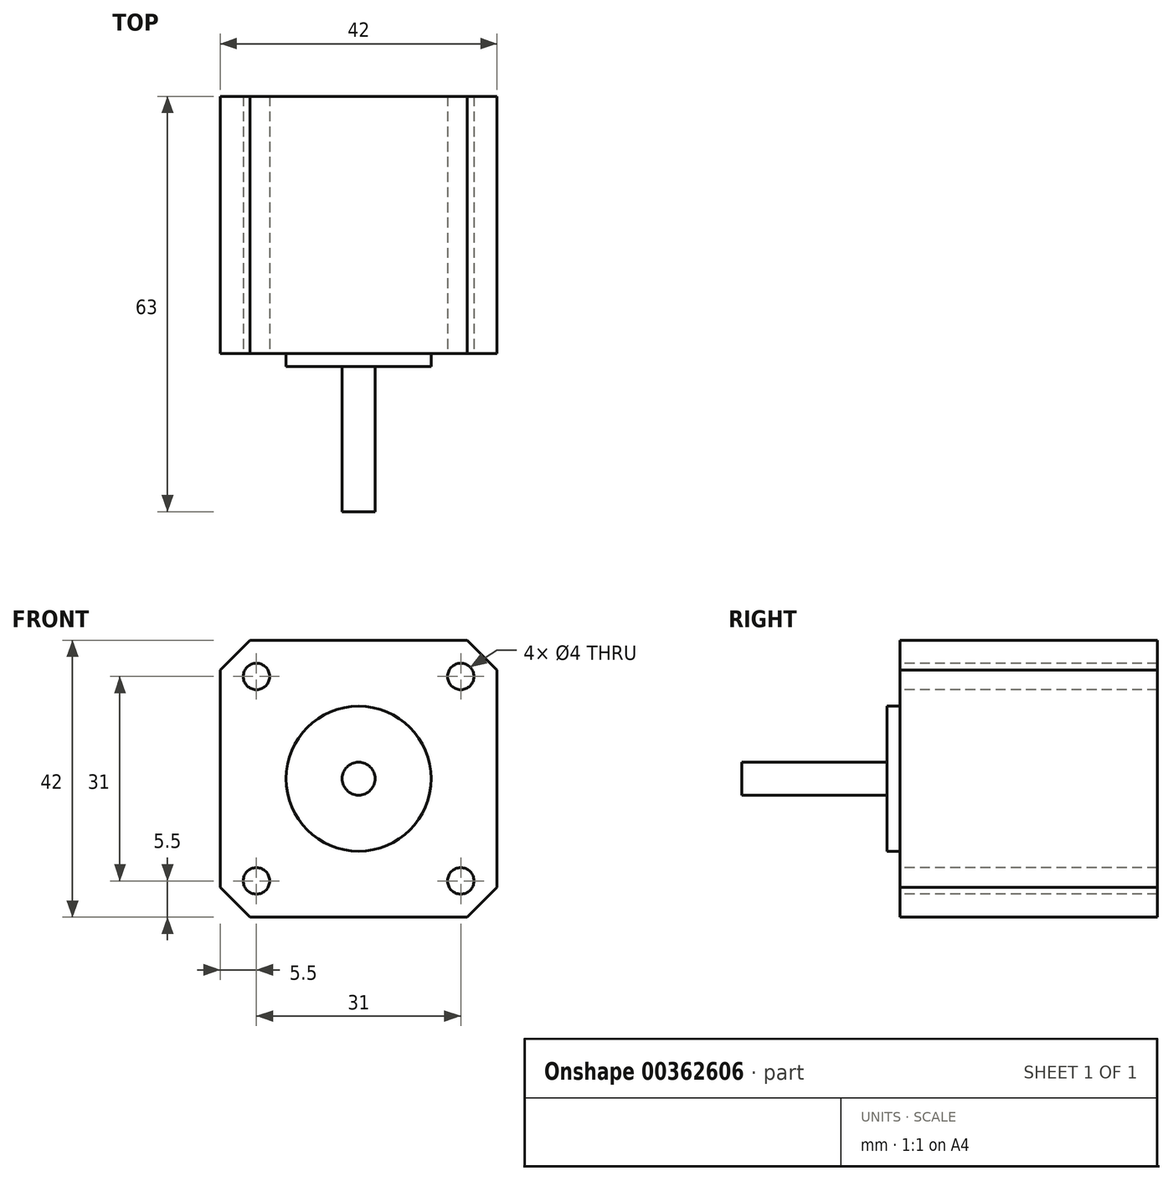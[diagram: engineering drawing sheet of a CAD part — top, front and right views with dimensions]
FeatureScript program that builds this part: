
annotation { "Feature Type Name" : "Feature", "Feature Type Description" : "" }
export const myFeature = defineFeature(function(context is Context, id is Id, definition is map)
    precondition{}
    {
        {
            var Q0;
            Q0=qCreatedBy(makeId("Front.planeOp"),FACE);
            var sketch = newSketch(context, id + "F0", { "sketchPlane" : qUnion([Q0])});
            skCircle(sketch, "E0", {"center": v(0, 0) * mm, "radius": 2.5 * mm});
            skSolve(sketch);
        }
        {
            var Q0;
            Q0=qCreatedBy(makeId("Front.planeOp"),FACE);
            var sketch = newSketch(context, id + "F1", { "sketchPlane" : qUnion([Q0])});
            skCircle(sketch, "E1", {"center": v(0, 0) * mm, "radius": 11 * mm});
            skSolve(sketch);
        }
        {
            var Q0;
            Q0=qCreatedBy(makeId("Front.planeOp"),FACE);
            var sketch = newSketch(context, id + "F2", { "sketchPlane" : qUnion([Q0])});
            skLineSegment(sketch, "E2.bottom", {"start": v(16.5, 21) * mm, "end": v(-16.5, 21) * mm});
            skLineSegment(sketch, "E2.top", {"start": v(16.5, -21) * mm, "end": v(-16.5, -21) * mm});
            skLineSegment(sketch, "E2.left", {"start": v(21, 16.5) * mm, "end": v(21, -16.5) * mm});
            skLineSegment(sketch, "E2.right", {"start": v(-21, 16.5) * mm, "end": v(-21, -16.5) * mm});
            skPoint(sketch, "E2.middle", {"position": v(0, 0) * mm});
            skPoint(sketch, "E3", {"position": v(-15.5, 15.5) * mm});
            skPoint(sketch, "E4", {"position": v(-15.5, -15.5) * mm});
            skPoint(sketch, "E5", {"position": v(15.5, 15.5) * mm});
            skPoint(sketch, "E6", {"position": v(15.5, -15.5) * mm});
            skLineSegment(sketch, "E7", {"start": v(-21, 16.5) * mm, "end": v(-16.5, 21) * mm});
            skLineSegment(sketch, "E8.MirrorCS", {"start": v(21, 16.5) * mm, "end": v(16.5, 21) * mm});
            skLineSegment(sketch, "E9.MirrorCS", {"start": v(-21, -16.5) * mm, "end": v(-16.5, -21) * mm});
            skLineSegment(sketch, "E10.MirrorCS", {"start": v(21, -16.5) * mm, "end": v(16.5, -21) * mm});
            skPoint(sketch, "E11.orphan", {"position": v(-21, 21) * mm});
            skPoint(sketch, "E12.orphan", {"position": v(21, 21) * mm});
            skPoint(sketch, "E13.orphan", {"position": v(21, -21) * mm});
            skPoint(sketch, "E14.orphan", {"position": v(-21, -21) * mm});
            skSolve(sketch);
        }
        {
            var Q0;
            Q0=qSketchRegion(id+"F0",true);
            extrude(context, id + "F3", {"entities" : qUnion([Q0]), "depth" : 24 * mm});
        }
        {
            var Q0;
            Q0=qSketchRegion(id+"F1",true);
            extrude(context, id + "F4", {"entities" : qUnion([Q0]), "operationType" : NewBodyOperationType.ADD, "depth" : 2 * mm});
        }
        {
            var Q0;
            Q0=qSketchRegion(id+"F2",true);
            extrude(context, id + "F5", {"entities" : qUnion([Q0]), "operationType" : NewBodyOperationType.ADD, "oppositeDirection" : true, "depth" : 39 * mm});
        }
        {
            var Q0;
            Q0=qCreatedBy(makeId("Front.planeOp"),FACE);
            var sketch = newSketch(context, id + "F6", { "sketchPlane" : qUnion([Q0])});
            skPoint(sketch, "E15", {"position": v(-15.5, 15.5) * mm});
            skPoint(sketch, "E16", {"position": v(-15.5, -15.5) * mm});
            skPoint(sketch, "E17", {"position": v(15.5, 15.5) * mm});
            skPoint(sketch, "E18", {"position": v(15.5, -15.5) * mm});
            skSolve(sketch);
        }
        {
            var Q0;
            Q0=sQuery(id+"F6.wireOp",VERTEX,"E15");
            var Q1;
            Q1=sQuery(id+"F6.wireOp",VERTEX,"E17");
            var Q2;
            Q2=sQuery(id+"F6.wireOp",VERTEX,"E18");
            var Q3;
            Q3=sQuery(id+"F6.wireOp",VERTEX,"E16");
            var Q4;
            Q4=makeQuery(id+"F3.opExtrude","SWEPT_BODY",BODY,{"disambiguationData":[OSD([sQuery(id+"F0.wireOp",EDGE,"E0")])]});
            hole(context, id + "F7", {"style" : HoleStyle.SIMPLE, "endStyle" : HoleEndStyle.THROUGH, "holeDiameter" : 4 * mm, "isTappedThrough" : true, "tappedDepth" : 12 * mm, "tapClearance" : 3, "locations" : qUnion([Q0, Q1, Q2, Q3]), "scope" : qUnion([Q4])});
        }
    });
